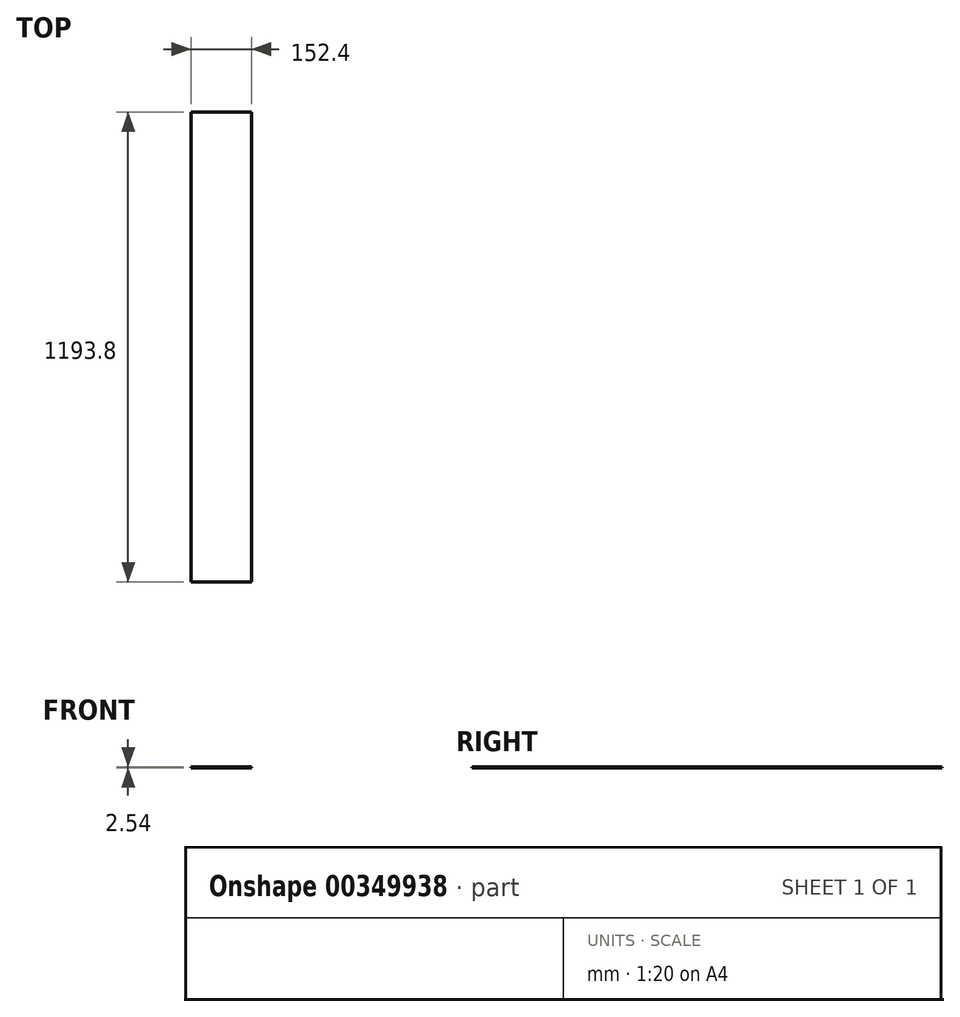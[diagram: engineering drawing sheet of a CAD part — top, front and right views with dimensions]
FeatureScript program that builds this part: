
annotation { "Feature Type Name" : "Feature", "Feature Type Description" : "" }
export const myFeature = defineFeature(function(context is Context, id is Id, definition is map)
    precondition{}
    {
        {
            var Q0;
            Q0=qCreatedBy(makeId("Top.planeOp"),FACE);
            var sketch = newSketch(context, id + "F0", { "sketchPlane" : qUnion([Q0])});
            skLineSegment(sketch, "E0.bottom", {"start": v(-42.56, -63.02) * mm, "end": v(109.84, -63.02) * mm});
            skLineSegment(sketch, "E0.top", {"start": v(-42.56, 1130.78) * mm, "end": v(109.84, 1130.78) * mm});
            skLineSegment(sketch, "E0.left", {"start": v(-42.56, -63.02) * mm, "end": v(-42.56, 1130.78) * mm});
            skLineSegment(sketch, "E0.right", {"start": v(109.84, -63.02) * mm, "end": v(109.84, 1130.78) * mm});
            skSolve(sketch);
        }
        {
            var Q0;
            Q0 = qSketchRegion(id + "F0", true);
            extrude(context, id + "F1", {"entities" : qUnion([Q0]), "depth" : 2.54 * mm, "offsetDistance" : 25.4 * mm});
        }
    });
